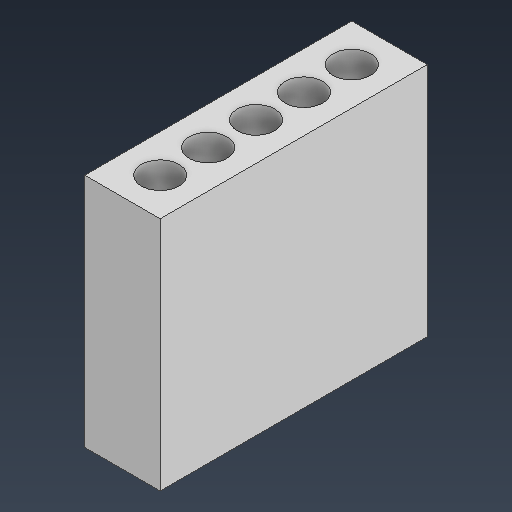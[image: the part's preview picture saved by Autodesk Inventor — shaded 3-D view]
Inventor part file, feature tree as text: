
AUTODESK INVENTOR PART (.ipt)
format: ipt  version: 2025.3 (Build 293356000, 356)  size: 112,128 bytes
history: native  units: mm
features: sketch x2, extrude x1
ambient origin geometry x8: Origin, YZ Plane, XZ Plane, XY Plane, X Axis, Y Axis, Z Axis, Center Point
bodies: Solid1 (feature_tree)
feature tree (3):
  extrude  "Extrusion1"  Depth=2.54mm
  sketch  "Sketch1"  dims[d0=2.0mm d1=50.0mm d3=2.54mm d4=10.0mm d6=10.0mm]
  sketch  "Sketch Rectangular Pattern1"  dims[d8=1.0mm d9=1.0mm d10=1.0mm d11=1.0mm d12=12.5mm d13=0.0mm]
